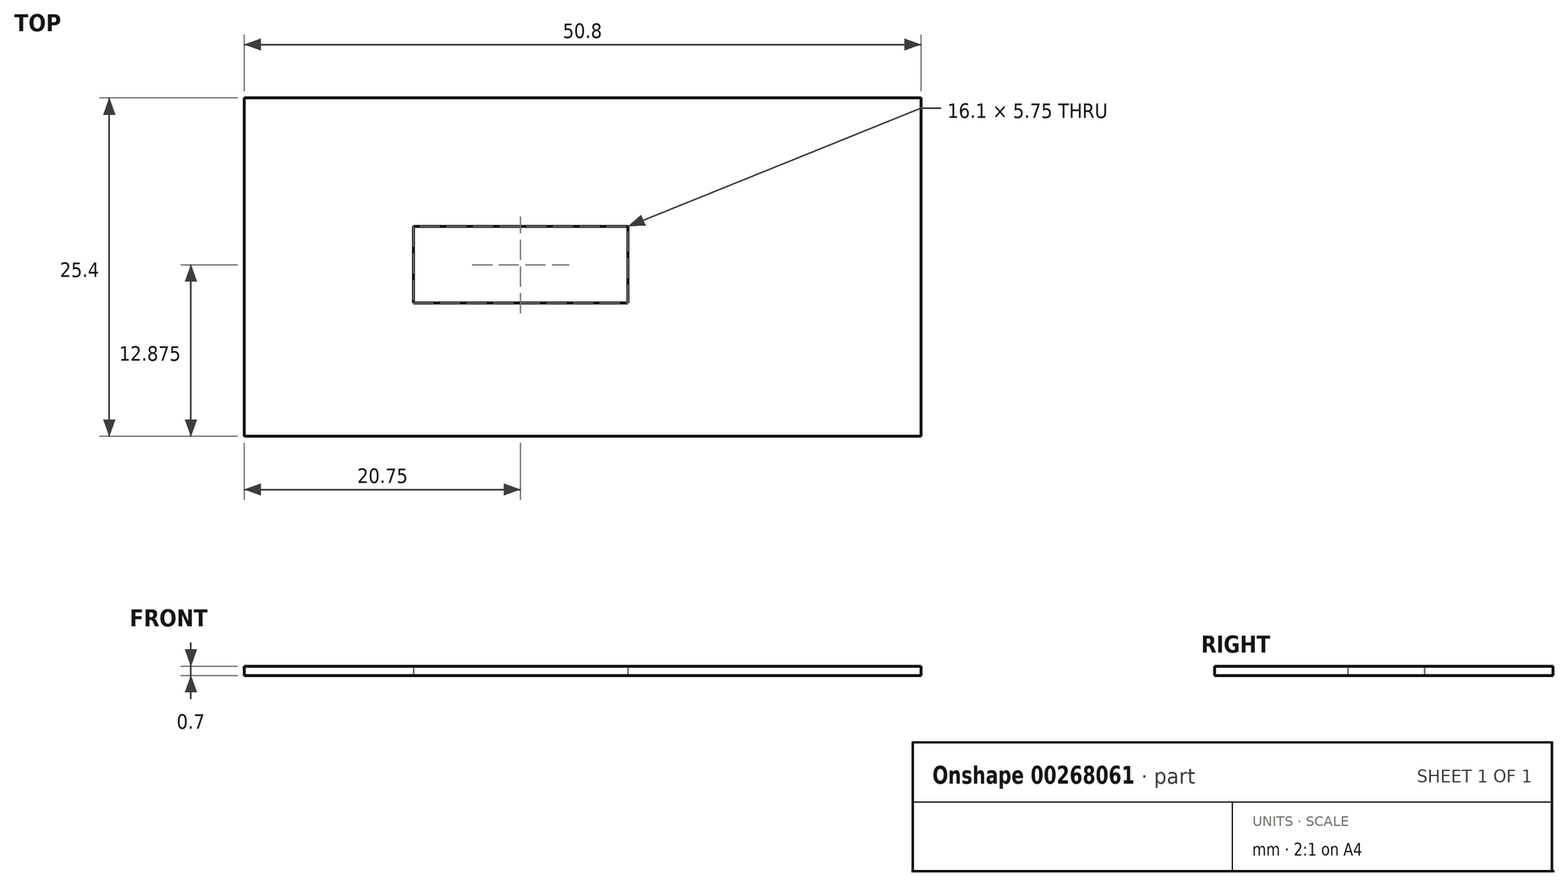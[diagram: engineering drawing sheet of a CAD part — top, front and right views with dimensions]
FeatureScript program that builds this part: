
annotation { "Feature Type Name" : "Feature", "Feature Type Description" : "" }
export const myFeature = defineFeature(function(context is Context, id is Id, definition is map)
    precondition{}
    {
        {
            var Q0;
            Q0=qCreatedBy(makeId("Top.planeOp"),FACE);
            var sketch = newSketch(context, id + "F0", { "sketchPlane" : qUnion([Q0])});
            skLineSegment(sketch, "E0", {"start": v(0, 0) * mm, "end": v(50.8, 0) * mm});
            skLineSegment(sketch, "E1.top", {"start": v(0, 25.4) * mm, "end": v(50.8, 25.4) * mm});
            skLineSegment(sketch, "E1.left", {"start": v(0, 0) * mm, "end": v(0, 25.4) * mm});
            skLineSegment(sketch, "E1.right", {"start": v(50.8, 0) * mm, "end": v(50.8, 25.4) * mm});
            skLineSegment(sketch, "E2.bottom", {"start": v(12.7, 10) * mm, "end": v(28.8, 10) * mm});
            skLineSegment(sketch, "E2.top", {"start": v(12.7, 15.75) * mm, "end": v(28.8, 15.75) * mm});
            skLineSegment(sketch, "E2.left", {"start": v(12.7, 10) * mm, "end": v(12.7, 15.75) * mm});
            skLineSegment(sketch, "E2.right", {"start": v(28.8, 10) * mm, "end": v(28.8, 15.75) * mm});
            skSolve(sketch);
        }
        {
            var Q0;
            Q0=makeQuery(id+"F0.imprint","IMPRINT",FACE,{"disambiguationData":[TD([[makeQuery(id+"F0.imprint","IMPRINT",EDGE,{"derivedFrom":sQuery(id+"F0.wireOp",EDGE,"E0")}),1.0]])]});
            extrude(context, id + "F1", {"entities" : qUnion([Q0]), "depth" : .7 * mm});
        }
    });
